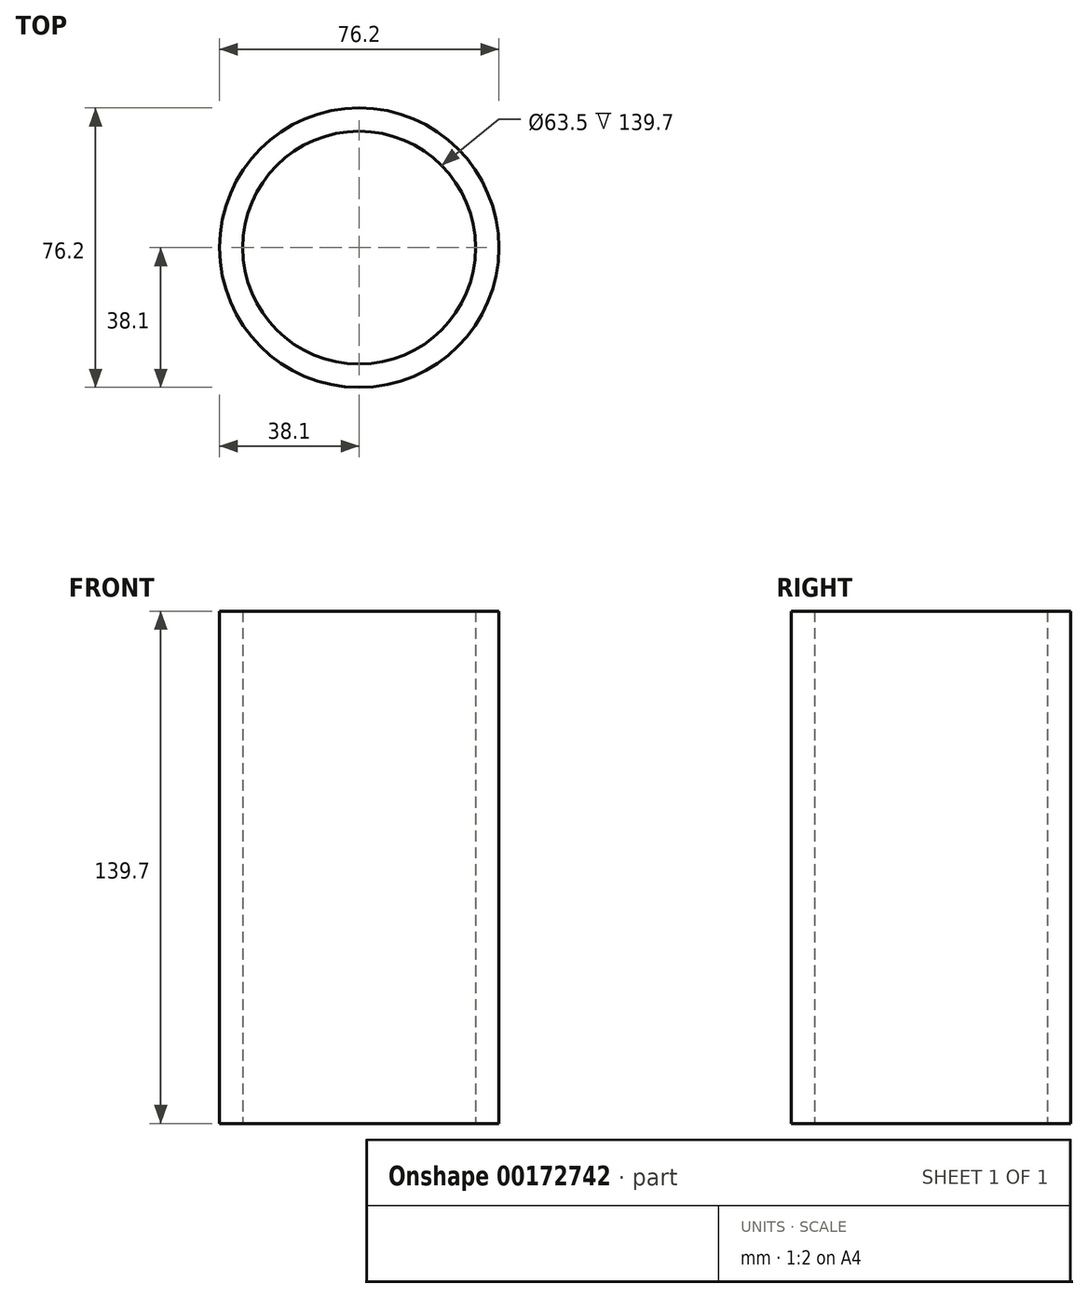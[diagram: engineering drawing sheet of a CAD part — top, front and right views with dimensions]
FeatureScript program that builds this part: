
annotation { "Feature Type Name" : "Feature", "Feature Type Description" : "" }
export const myFeature = defineFeature(function(context is Context, id is Id, definition is map)
    precondition{}
    {
        {
            var Q0;
            Q0=qCreatedBy(makeId("Top.planeOp"),FACE);
            var sketch = newSketch(context, id + "F0", { "sketchPlane" : qUnion([Q0])});
            skCircle(sketch, "E0", {"center": v(0, 0) * mm, "radius": 38.1 * mm});
            skCircle(sketch, "E1", {"center": v(0, 0) * mm, "radius": 31.75 * mm});
            skSolve(sketch);
        }
        {
            var Q0;
            Q0=makeQuery(id+"F0.imprint","IMPRINT",FACE,{"disambiguationData":[TD([[makeQuery(id+"F0.imprint","IMPRINT",EDGE,{"derivedFrom":sQuery(id+"F0.wireOp",EDGE,"E0")}),1.0]])]});
            extrude(context, id + "F1", {"entities" : qUnion([Q0]), "depth" : 139.7 * mm});
        }
    });
